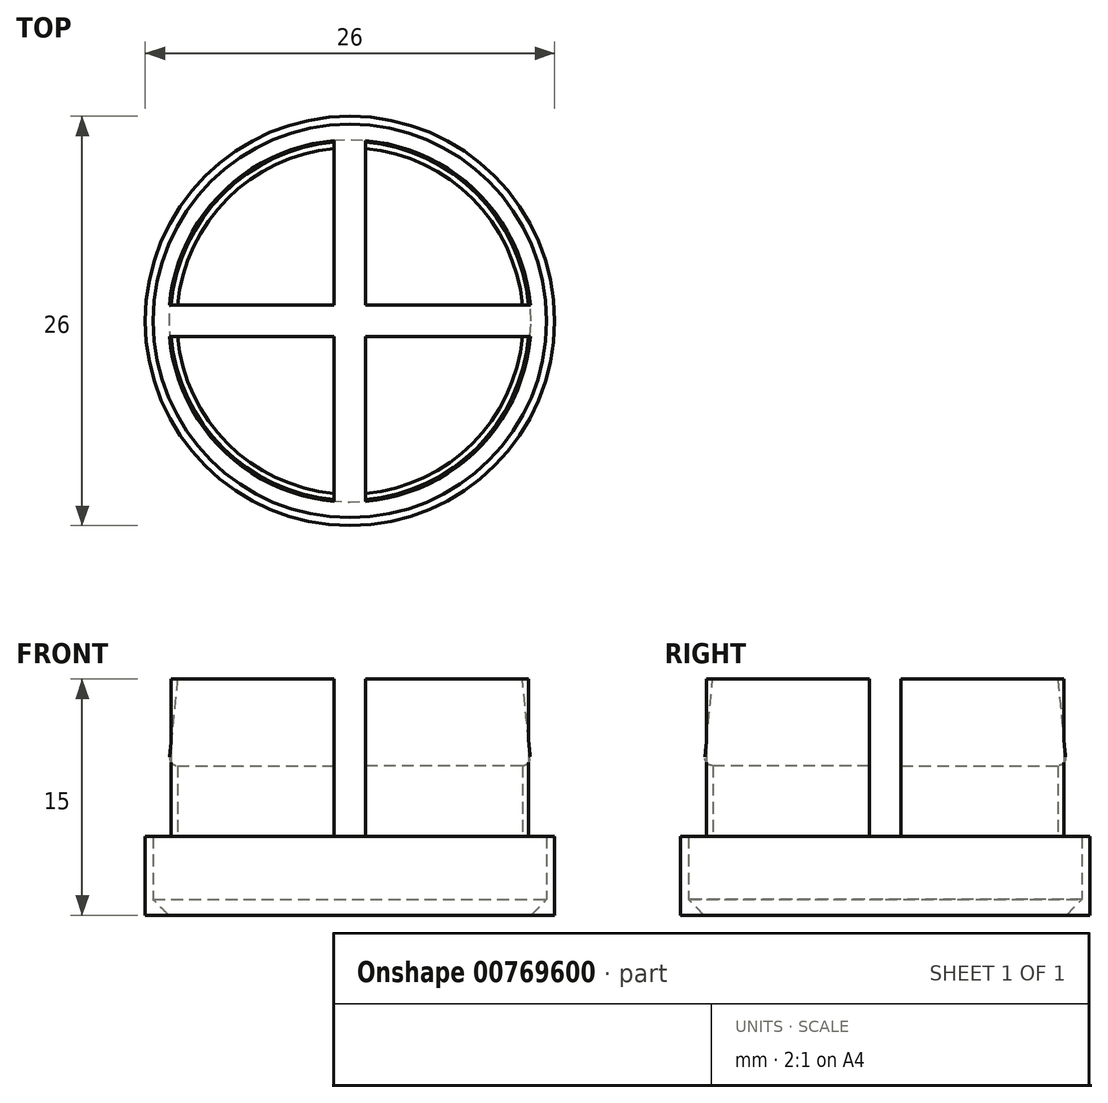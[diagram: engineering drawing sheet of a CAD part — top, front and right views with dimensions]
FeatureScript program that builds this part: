
annotation { "Feature Type Name" : "Feature", "Feature Type Description" : "" }
export const myFeature = defineFeature(function(context is Context, id is Id, definition is map)
    precondition{}
    {
        {
            var Q0;
            Q0=qCreatedBy(makeId("Top.planeOp"),FACE);
            var sketch = newSketch(context, id + "F0", { "sketchPlane" : qUnion([Q0])});
            skCircle(sketch, "E0", {"center": v(0, 0) * mm, "radius": 13 * mm});
            skSolve(sketch);
        }
        {
            var Q0;
            Q0=qSketchRegion(id+"F0",true);
            extrude(context, id + "F1", {"entities" : qUnion([Q0]), "depth" : 5 * mm, "offsetDistance" : 25 * mm});
        }
        {
            var Q0;
            Q0=makeQuery(id+"F1.opExtrude","CAP_FACE",FACE,{"disambiguationData":[OSD([sQuery(id+"F0.wireOp",EDGE,"E0")])],"isStart":false});
            var sketch = newSketch(context, id + "F2", { "sketchPlane" : qUnion([Q0])});
            skCircle(sketch, "E1", {"center": v(0, 0) * mm, "radius": 11.4 * mm});
            skSolve(sketch);
        }
        {
            var Q0;
            Q0=qSketchRegion(id+"F2",true);
            extrude(context, id + "F3", {"entities" : qUnion([Q0]), "operationType" : NewBodyOperationType.ADD, "depth" : 10 * mm, "offsetDistance" : 25 * mm});
        }
        {
            var Q0;
            Q0=qCreatedBy(makeId("Front.planeOp"),FACE);
            var sketch = newSketch(context, id + "F4", { "sketchPlane" : qUnion([Q0])});
            skLineSegment(sketch, "E2.bottom", {"start": v(0, 0) * mm, "end": v(-12.5, 0) * mm});
            skLineSegment(sketch, "E2.top", {"start": v(-11, 5) * mm, "end": v(-12.5, 5) * mm});
            skLineSegment(sketch, "E2.left", {"start": v(0, 0) * mm, "end": v(0, 5) * mm});
            skLineSegment(sketch, "E2.right", {"start": v(-12.5, 0) * mm, "end": v(-12.5, 5) * mm});
            skLineSegment(sketch, "E3.top", {"start": v(0, 15) * mm, "end": v(-11, 15) * mm});
            skLineSegment(sketch, "E3.left", {"start": v(0, 5) * mm, "end": v(0, 15) * mm});
            skLineSegment(sketch, "E3.right", {"start": v(-11, 5) * mm, "end": v(-11, 9.5) * mm});
            skArc(sketch, "E4", {"start": v(-11.5, 10.05) * mm, "mid": v(-11.37, 9.66) * mm, "end": v(-11, 9.5) * mm});
            skLineSegment(sketch, "E5", {"start": v(-11, 15) * mm, "end": v(-11.5, 10.05) * mm});
            skSolve(sketch);
        }
        {
            var Q0;
            Q0 = qSketchRegion(id + "F4", true);
            var Q1;
            Q1=sQuery(id+"F4.wireOp",EDGE,"E2.left");
            revolve(context, id + "F5", {"surfaceOperationType" : NewSurfaceOperationType.NEW, "entities" : qUnion([Q0]), "axis" : qUnion([Q1]), "revolveType" : RevolveType.FULL});
        }
        {
            var Q0;
            Q0=makeQuery(id+"F5.opRevolve","SWEPT_FACE",FACE,{"disambiguationData":[OSD([sQuery(id+"F4.wireOp",EDGE,"E3.top")])]});
            var sketch = newSketch(context, id + "F6", { "sketchPlane" : qUnion([Q0])});
            skLineSegment(sketch, "E6.bottom", {"start": v(-13, 1) * mm, "end": v(-1, 1) * mm});
            skLineSegment(sketch, "E6.top", {"start": v(-13, -1) * mm, "end": v(-1, -1) * mm});
            skLineSegment(sketch, "E6.left", {"start": v(-13, 1) * mm, "end": v(-13, -1) * mm});
            skLineSegment(sketch, "E6.right", {"start": v(13, 1) * mm, "end": v(13, -1) * mm});
            skPoint(sketch, "E6.middle", {"position": v(0, 0) * mm});
            skLineSegment(sketch, "E7.bottom", {"start": v(1, 13) * mm, "end": v(-1, 13) * mm});
            skLineSegment(sketch, "E7.top", {"start": v(1, -13) * mm, "end": v(-1, -13) * mm});
            skLineSegment(sketch, "E7.left", {"start": v(1, 13) * mm, "end": v(1, 1) * mm});
            skLineSegment(sketch, "E7.right", {"start": v(-1, 13) * mm, "end": v(-1, 1) * mm});
            skLineSegment(sketch, "E8.trimOffspring", {"start": v(1, 1) * mm, "end": v(13, 1) * mm});
            skLineSegment(sketch, "E9.trimOffspring", {"start": v(-1, -1) * mm, "end": v(-1, -13) * mm});
            skLineSegment(sketch, "E10.trimOffspring", {"start": v(1, -1) * mm, "end": v(1, -13) * mm});
            skLineSegment(sketch, "E11.trimOffspring", {"start": v(1, -1) * mm, "end": v(13, -1) * mm});
            skSolve(sketch);
        }
        {
            var Q0;
            Q0 = qSketchRegion(id + "F6", true);
            extrude(context, id + "F7", {"entities" : qUnion([Q0]), "operationType" : NewBodyOperationType.REMOVE, "oppositeDirection" : true, "depth" : 10 * mm, "offsetDistance" : 25 * mm});
        }
        {
            var Q0;
            Q0=makeQuery(id+"F5.opRevolve","SWEPT_FACE",FACE,{"disambiguationData":[OSD([sQuery(id+"F4.wireOp",EDGE,"E2.bottom")])]});
            chamfer(context, id + "F8", {"entities" : qUnion([Q0]), "width" : 1 * mm, "tangentPropagation" : true});
        }
    });
